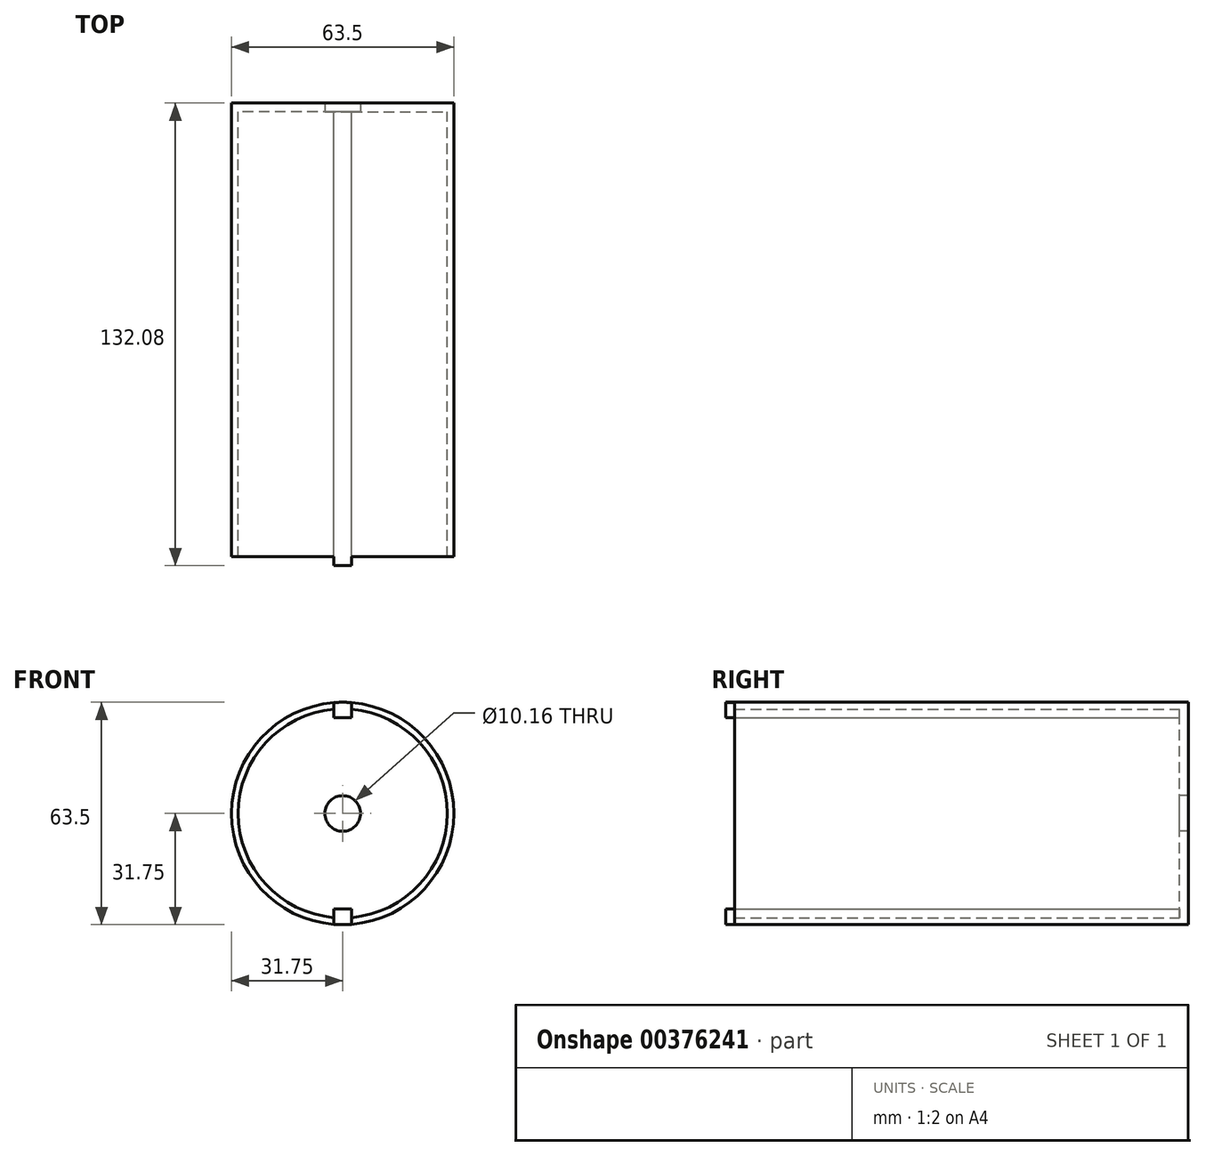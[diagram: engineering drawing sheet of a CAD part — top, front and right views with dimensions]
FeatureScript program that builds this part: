
annotation { "Feature Type Name" : "Feature", "Feature Type Description" : "" }
export const myFeature = defineFeature(function(context is Context, id is Id, definition is map)
    precondition{}
    {
        {
            var Q0;
            Q0=qCreatedBy(makeId("Front.planeOp"),FACE);
            var sketch = newSketch(context, id + "F0", { "sketchPlane" : qUnion([Q0])});
            skCircle(sketch, "E0", {"center": v(0, 0) * mm, "radius": 31.75 * mm});
            skCircle(sketch, "E1", {"center": v(0, 0) * mm, "radius": 29.85 * mm});
            skLineSegment(sketch, "E2", {"start": v(0, -29.85) * mm, "end": v(0, -27.3) * mm});
            skLineSegment(sketch, "E3", {"start": v(0, -27.3) * mm, "end": v(2.54, -27.3) * mm});
            skLineSegment(sketch, "E4", {"start": v(2.54, -27.3) * mm, "end": v(2.54, -29.74) * mm});
            skLineSegment(sketch, "E5", {"start": v(0, -27.3) * mm, "end": v(-2.54, -27.3) * mm});
            skLineSegment(sketch, "E6", {"start": v(-2.54, -27.3) * mm, "end": v(-2.54, -29.74) * mm});
            skLineSegment(sketch, "E7", {"start": v(0, 29.85) * mm, "end": v(0, 27.3) * mm});
            skLineSegment(sketch, "E8", {"start": v(0, 27.3) * mm, "end": v(2.54, 27.3) * mm});
            skLineSegment(sketch, "E9", {"start": v(2.54, 27.3) * mm, "end": v(2.54, 29.74) * mm});
            skLineSegment(sketch, "E10", {"start": v(0, 27.3) * mm, "end": v(-2.54, 27.3) * mm});
            skLineSegment(sketch, "E11", {"start": v(-2.54, 27.3) * mm, "end": v(-2.54, 29.85) * mm});
            skSolve(sketch);
        }
        {
            var Q0;
            Q0=makeQuery(id+"F0.imprint","IMPRINT",FACE,{"disambiguationData":[TD([[makeQuery(id+"F0.imprint","IMPRINT",EDGE,{"derivedFrom":sQuery(id+"F0.wireOp",EDGE,"E0")}),1.0]])]});
            var Q1;
            {var subQ0=sQuery(id+"F0.wireOp",EDGE,"E7");Q1=makeQuery(id+"F0.imprint","IMPRINT",FACE,{"disambiguationData":[TD([[makeQuery(id+"F0.imprint","IMPRINT",EDGE,{"derivedFrom":subQ0}),-1.0]])]});}
            var Q2;
            {var subQ0=sQuery(id+"F0.wireOp",EDGE,"E7");Q2=makeQuery(id+"F0.imprint","IMPRINT",FACE,{"disambiguationData":[TD([[makeQuery(id+"F0.imprint","IMPRINT",EDGE,{"derivedFrom":subQ0}),1.0]])]});}
            var Q3;
            {var subQ0=sQuery(id+"F0.wireOp",EDGE,"E2");Q3=makeQuery(id+"F0.imprint","IMPRINT",FACE,{"disambiguationData":[TD([[makeQuery(id+"F0.imprint","IMPRINT",EDGE,{"derivedFrom":subQ0}),1.0]])]});}
            var Q4;
            {var subQ0=sQuery(id+"F0.wireOp",EDGE,"E2");Q4=makeQuery(id+"F0.imprint","IMPRINT",FACE,{"disambiguationData":[TD([[makeQuery(id+"F0.imprint","IMPRINT",EDGE,{"derivedFrom":subQ0}),-1.0]])]});}
            var Q5;
            Q5=sQuery(id+"F0.wireOp",EDGE,"E0");
            extrude(context, id + "F1", {"entities" : qUnion([Q0, Q1, Q2, Q3, Q4]), "surfaceEntities" : qUnion([Q5]), "depth" : 127 * mm});
        }
        {
            var Q0;
            Q0=qCreatedBy(makeId("Front.planeOp"),FACE);
            var sketch = newSketch(context, id + "F2", { "sketchPlane" : qUnion([Q0])});
            skCircle(sketch, "E12", {"center": v(0, 0) * mm, "radius": 31.75 * mm});
            skCircle(sketch, "E13", {"center": v(0, 0) * mm, "radius": 5.08 * mm});
            skSolve(sketch);
        }
        {
            var Q0;
            Q0=makeQuery(id+"F2.imprint","IMPRINT",FACE,{"disambiguationData":[TD([[makeQuery(id+"F2.imprint","IMPRINT",EDGE,{"derivedFrom":sQuery(id+"F2.wireOp",EDGE,"E12")}),1.0]])]});
            extrude(context, id + "F3", {"entities" : qUnion([Q0]), "oppositeDirection" : true, "depth" : 2.54 * mm});
        }
        {
            var Q0;
            Q0=makeQuery(id+"F3.opExtrude","CAP_FACE",FACE,{"disambiguationData":[OSD([sQuery(id+"F2.wireOp",EDGE,"E12"),sQuery(id+"F2.wireOp",EDGE,"E13")])],"isStart":false});
            var sketch = newSketch(context, id + "F4", { "sketchPlane" : qUnion([Q0])});
            skCircle(sketch, "E14", {"center": v(0, 0) * mm, "radius": 31.75 * mm});
            skLineSegment(sketch, "E15", {"start": v(0, 31.75) * mm, "end": v(0, 27.3) * mm});
            skLineSegment(sketch, "E16", {"start": v(0, 27.3) * mm, "end": v(2.54, 27.3) * mm});
            skLineSegment(sketch, "E17", {"start": v(2.54, 27.3) * mm, "end": v(2.54, 31.65) * mm});
            skLineSegment(sketch, "E18", {"start": v(0, 27.3) * mm, "end": v(-2.54, 27.3) * mm});
            skLineSegment(sketch, "E19", {"start": v(-2.54, 27.3) * mm, "end": v(-2.54, 31.65) * mm});
            skLineSegment(sketch, "E20", {"start": v(0, 0) * mm, "end": v(1.56, 0) * mm});
            skLineSegment(sketch, "E21.MirrorCS", {"start": v(0, -27.3) * mm, "end": v(2.54, -27.3) * mm});
            skLineSegment(sketch, "E22.MirrorCS", {"start": v(0, -27.3) * mm, "end": v(-2.54, -27.3) * mm});
            skLineSegment(sketch, "E23.MirrorCS", {"start": v(-2.54, -27.3) * mm, "end": v(-2.54, -31.65) * mm});
            skLineSegment(sketch, "E24.MirrorCS", {"start": v(2.54, -27.3) * mm, "end": v(2.54, -31.65) * mm});
            skSolve(sketch);
        }
        {
            var Q0;
            Q0=makeQuery(id+"F4.imprint","IMPRINT",FACE,{"disambiguationData":[TD([[makeQuery(id+"F4.imprint","IMPRINT",EDGE,{"derivedFrom":sQuery(id+"F4.wireOp",EDGE,"E21.MirrorCS")}),-1.0]])]});
            var Q1;
            {var subQ0=sQuery(id+"F4.wireOp",EDGE,"E15");Q1=makeQuery(id+"F4.imprint","IMPRINT",FACE,{"disambiguationData":[TD([[makeQuery(id+"F4.imprint","IMPRINT",EDGE,{"derivedFrom":subQ0}),-1.0]])]});}
            var Q2;
            {var subQ0=sQuery(id+"F4.wireOp",EDGE,"E15");Q2=makeQuery(id+"F4.imprint","IMPRINT",FACE,{"disambiguationData":[TD([[makeQuery(id+"F4.imprint","IMPRINT",EDGE,{"derivedFrom":subQ0}),1.0]])]});}
            extrude(context, id + "F5", {"entities" : qUnion([Q0, Q1, Q2]), "operationType" : NewBodyOperationType.REMOVE, "oppositeDirection" : true, "depth" : 2.54 * mm});
        }
        {
            var Q0;
            Q0=makeQuery(id+"F1.opExtrude","CAP_FACE",FACE,{"disambiguationData":[OSD([sQuery(id+"F0.wireOp",EDGE,"E0"),sQuery(id+"F0.wireOp",EDGE,"E1"),sQuery(id+"F0.wireOp",EDGE,"E3"),sQuery(id+"F0.wireOp",EDGE,"E4"),sQuery(id+"F0.wireOp",EDGE,"E5"),sQuery(id+"F0.wireOp",EDGE,"E6"),sQuery(id+"F0.wireOp",EDGE,"E8"),sQuery(id+"F0.wireOp",EDGE,"E9"),sQuery(id+"F0.wireOp",EDGE,"E10"),sQuery(id+"F0.wireOp",EDGE,"E11")])],"isStart":true});
            var sketch = newSketch(context, id + "F6", { "sketchPlane" : qUnion([Q0])});
            skLineSegment(sketch, "E25", {"start": v(-2.54, 27.3) * mm, "end": v(-2.54, 31.65) * mm});
            skLineSegment(sketch, "E26", {"start": v(-2.54, 27.3) * mm, "end": v(2.54, 27.3) * mm});
            skLineSegment(sketch, "E27", {"start": v(2.54, 27.3) * mm, "end": v(2.54, 31.65) * mm});
            skCircle(sketch, "E28", {"center": v(0, 0) * mm, "radius": 31.75 * mm});
            skLineSegment(sketch, "E29", {"start": v(-2.54, -27.3) * mm, "end": v(-2.54, -31.65) * mm});
            skLineSegment(sketch, "E30", {"start": v(-2.54, -27.3) * mm, "end": v(2.54, -27.3) * mm});
            skLineSegment(sketch, "E31", {"start": v(2.54, -27.3) * mm, "end": v(2.54, -31.65) * mm});
            skSolve(sketch);
        }
        {
            var Q0;
            {var subQ1=sQuery(id+"F6.wireOp",EDGE,"E26");Q0=makeQuery(id+"F6.imprint","IMPRINT",FACE,{"disambiguationData":[TD([[makeQuery(id+"F6.imprint","IMPRINT",EDGE,{"derivedFrom":subQ1}),1.0]])]});}
            var Q1;
            {var subQ0=sQuery(id+"F6.wireOp",EDGE,"E30");Q1=makeQuery(id+"F6.imprint","IMPRINT",FACE,{"disambiguationData":[TD([[makeQuery(id+"F6.imprint","IMPRINT",EDGE,{"derivedFrom":subQ0}),-1.0]])]});}
            extrude(context, id + "F7", {"entities" : qUnion([Q0, Q1]), "operationType" : NewBodyOperationType.ADD, "depth" : 2.54 * mm});
        }
        {
            var Q0;
            Q0=makeQuery(id+"F1.opExtrude","CAP_FACE",FACE,{"disambiguationData":[OSD([sQuery(id+"F0.wireOp",EDGE,"E0"),sQuery(id+"F0.wireOp",EDGE,"E1"),sQuery(id+"F0.wireOp",EDGE,"E3"),sQuery(id+"F0.wireOp",EDGE,"E4"),sQuery(id+"F0.wireOp",EDGE,"E5"),sQuery(id+"F0.wireOp",EDGE,"E6"),sQuery(id+"F0.wireOp",EDGE,"E8"),sQuery(id+"F0.wireOp",EDGE,"E9"),sQuery(id+"F0.wireOp",EDGE,"E10"),sQuery(id+"F0.wireOp",EDGE,"E11")])],"isStart":false});
            var sketch = newSketch(context, id + "F8", { "sketchPlane" : qUnion([Q0])});
            skCircle(sketch, "E32", {"center": v(0, 0) * mm, "radius": 31.75 * mm});
            skLineSegment(sketch, "E33", {"start": v(-2.54, 27.3) * mm, "end": v(-2.54, 31.65) * mm});
            skLineSegment(sketch, "E34", {"start": v(-2.54, 27.3) * mm, "end": v(2.54, 27.3) * mm});
            skLineSegment(sketch, "E35", {"start": v(2.54, 27.3) * mm, "end": v(2.54, 31.65) * mm});
            skLineSegment(sketch, "E36", {"start": v(-2.54, -27.3) * mm, "end": v(-2.54, -31.65) * mm});
            skPoint(sketch, "E36.endSnap0", {"position": v(-2.54, -28.52) * mm});
            skLineSegment(sketch, "E37", {"start": v(-2.54, -27.3) * mm, "end": v(2.54, -27.3) * mm});
            skLineSegment(sketch, "E38", {"start": v(2.54, -27.3) * mm, "end": v(2.54, -31.65) * mm});
            skSolve(sketch);
        }
        {
            var Q0;
            {var subQ0=sQuery(id+"F8.wireOp",EDGE,"E37");Q0=makeQuery(id+"F8.imprint","IMPRINT",FACE,{"disambiguationData":[TD([[makeQuery(id+"F8.imprint","IMPRINT",EDGE,{"derivedFrom":subQ0}),1.0]])]});}
            var Q1;
            {var subQ0=sQuery(id+"F8.wireOp",EDGE,"E34");Q1=makeQuery(id+"F8.imprint","IMPRINT",FACE,{"disambiguationData":[TD([[makeQuery(id+"F8.imprint","IMPRINT",EDGE,{"derivedFrom":subQ0}),-1.0]])]});}
            extrude(context, id + "F9", {"entities" : qUnion([Q0, Q1]), "operationType" : NewBodyOperationType.ADD, "depth" : 2.54 * mm});
        }
    });
